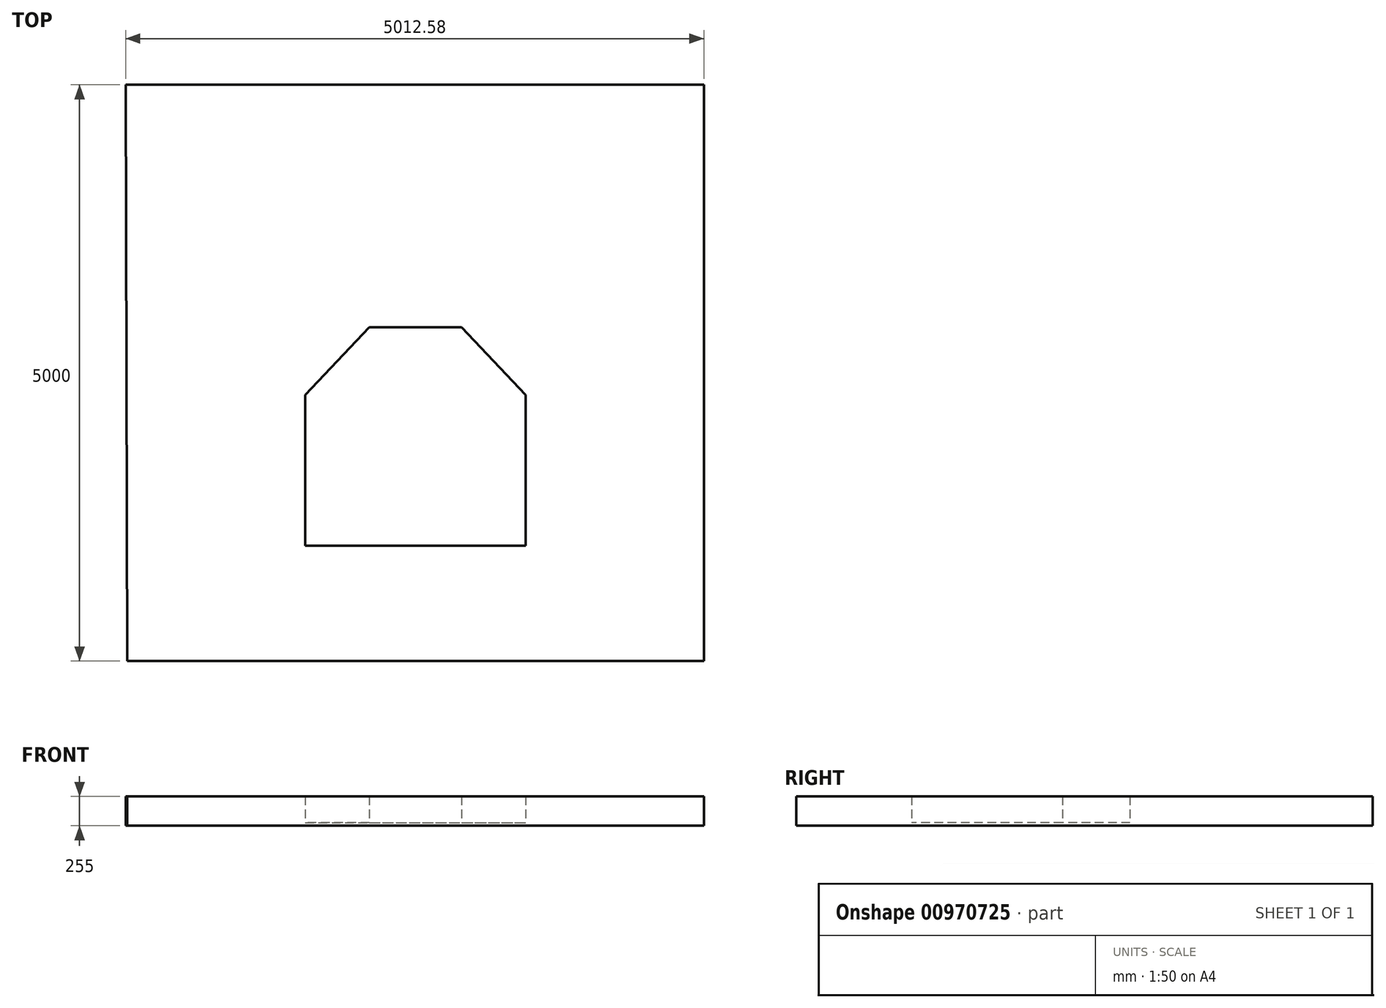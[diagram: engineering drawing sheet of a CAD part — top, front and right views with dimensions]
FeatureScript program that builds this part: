
annotation { "Feature Type Name" : "Feature", "Feature Type Description" : "" }
export const myFeature = defineFeature(function(context is Context, id is Id, definition is map)
    precondition{}
    {
        {
            var Q0;
            Q0=qCreatedBy(makeId("Top.planeOp"),FACE);
            var sketch = newSketch(context, id + "F0", { "sketchPlane" : qUnion([Q0])});
            skLineSegment(sketch, "E0.top", {"start": v(-2500, -1512.17) * mm, "end": v(2500, -1512.17) * mm});
            skArc(sketch, "E1.filletArc", {"start": v(-2512.58, 3487.83) * mm, "mid": v(-2516.03, 3486.32) * mm, "end": v(-2517.44, 3482.83) * mm});
            skLineSegment(sketch, "E2.bottom", {"start": v(-400, 1382.83) * mm, "end": v(400, 1382.83) * mm});
            skLineSegment(sketch, "E2.top", {"start": v(-956, -512.17) * mm, "end": v(956, -512.17) * mm});
            skLineSegment(sketch, "E2.left", {"start": v(-956, 796.83) * mm, "end": v(-956, -512.17) * mm});
            skLineSegment(sketch, "E2.right", {"start": v(956, 796.83) * mm, "end": v(956, -512.17) * mm});
            skLineSegment(sketch, "E3", {"start": v(0, 1382.83) * mm, "end": v(-400, 1382.83) * mm});
            skLineSegment(sketch, "E4", {"start": v(-400, 1382.83) * mm, "end": v(-956, 796.83) * mm});
            skLineSegment(sketch, "E5.MirrorCS", {"start": v(0, 1382.83) * mm, "end": v(400, 1382.83) * mm});
            skLineSegment(sketch, "E6.MirrorCS", {"start": v(400, 1382.83) * mm, "end": v(956, 796.83) * mm});
            skPoint(sketch, "E7.orphan", {"position": v(-956, 1382.83) * mm});
            skPoint(sketch, "E8.orphan", {"position": v(956, 1382.83) * mm});
            skLineSegment(sketch, "E9", {"start": v(-2512.58, 3487.83) * mm, "end": v(2500, 3487.83) * mm});
            skLineSegment(sketch, "E10", {"start": v(-2512.58, 3487.83) * mm, "end": v(-2500, -1512.17) * mm});
            skLineSegment(sketch, "E11", {"start": v(2500, -1512.17) * mm, "end": v(2500, 3487.83) * mm});
            skSolve(sketch);
        }
        {
            var Q0;
            {var subQ1=sQuery(id+"F0.wireOp",EDGE,"E0.left");Q0=makeQuery(id+"F0.imprint","IMPRINT",FACE,{"disambiguationData":[TD([[makeQuery(id+"F0.imprint","IMPRINT",EDGE,{"derivedFrom":subQ1}),1.0]])]});}
            var Q1;
            Q1=makeQuery(id+"F0.imprint","IMPRINT",FACE,{"disambiguationData":[TD([[makeQuery(id+"F0.imprint","IMPRINT",EDGE,{"derivedFrom":sQuery(id+"F0.wireOp",EDGE,"E2.top")}),-1.0]])]});
            extrude(context, id + "F1", {"entities" : qUnion([Q0, Q1]), "depth" : 230 * mm, "offsetDistance" : 25 * mm});
        }
        {
            var Q0;
            Q0=makeQuery(id+"F0.imprint","IMPRINT",FACE,{"disambiguationData":[TD([[makeQuery(id+"F0.imprint","IMPRINT",EDGE,{"derivedFrom":sQuery(id+"F0.wireOp",EDGE,"E2.top")}),-1.0]])]});
            var Q1;
            Q1=makeQuery(id+"F0.imprint","IMPRINT",FACE,{"disambiguationData":[TD([[makeQuery(id+"F0.imprint","IMPRINT",EDGE,{"derivedFrom":sQuery(id+"F0.wireOp",EDGE,"E2.top")}),1.0]])]});
            extrude(context, id + "F2", {"entities" : qUnion([Q0, Q1]), "operationType" : NewBodyOperationType.ADD, "oppositeDirection" : true, "depth" : 25 * mm, "offsetDistance" : 25 * mm});
        }
    });
